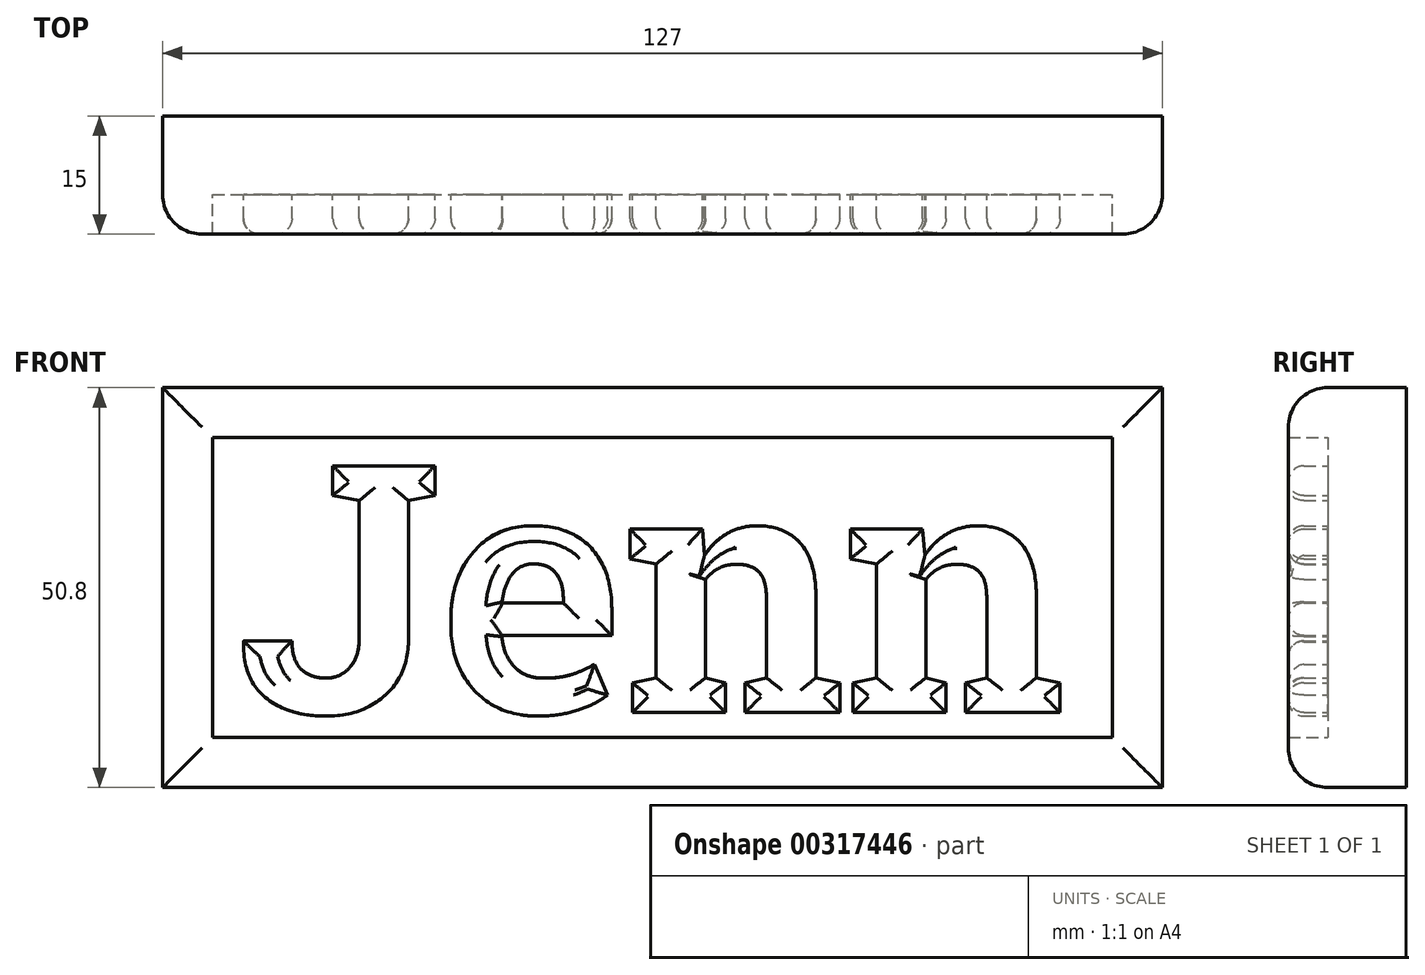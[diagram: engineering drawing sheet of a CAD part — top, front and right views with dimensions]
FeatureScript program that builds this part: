
annotation { "Feature Type Name" : "Feature", "Feature Type Description" : "" }
export const myFeature = defineFeature(function(context is Context, id is Id, definition is map)
    precondition{}
    {
        {
            var Q0;
            Q0=qCreatedBy(makeId("Front.planeOp"),FACE);
            var sketch = newSketch(context, id + "F0", { "sketchPlane" : qUnion([Q0])});
            skText(sketch, "E0", { "text": "Jenn", "fontName": "RobotoSlab-Bold.ttf"});
            const initialGuessF0  = {"E0": [-0.05398, -0.01588, 1, 0, 0.03175]};
            skSetInitialGuess(sketch, initialGuessF0);
            skSolve(sketch);
        }
        {
            var Q0;
            Q0=qCreatedBy(makeId("Front.planeOp"),FACE);
            var sketch = newSketch(context, id + "F1", { "sketchPlane" : qUnion([Q0])});
            skLineSegment(sketch, "E1.bottom", {"start": v(-57.15, 19.05) * mm, "end": v(57.15, 19.05) * mm});
            skLineSegment(sketch, "E1.top", {"start": v(-57.15, -19.05) * mm, "end": v(57.15, -19.05) * mm});
            skLineSegment(sketch, "E1.left", {"start": v(-57.15, 19.05) * mm, "end": v(-57.15, -19.05) * mm});
            skLineSegment(sketch, "E1.right", {"start": v(57.15, 19.05) * mm, "end": v(57.15, -19.05) * mm});
            skLineSegment(sketch, "E2.bottom", {"start": v(-63.5, 25.4) * mm, "end": v(63.5, 25.4) * mm});
            skLineSegment(sketch, "E2.top", {"start": v(-63.5, -25.4) * mm, "end": v(63.5, -25.4) * mm});
            skLineSegment(sketch, "E2.left", {"start": v(-63.5, 25.4) * mm, "end": v(-63.5, -25.4) * mm});
            skLineSegment(sketch, "E2.right", {"start": v(63.5, 25.4) * mm, "end": v(63.5, -25.4) * mm});
            skSolve(sketch);
        }
        {
            var Q0;
            Q0=makeQuery(id+"F1.imprint","IMPRINT",FACE,{"disambiguationData":[TD([[makeQuery(id+"F1.imprint","IMPRINT",EDGE,{"derivedFrom":sQuery(id+"F1.wireOp",EDGE,"E1.bottom")}),-1.0]])]});
            var Q1;
            Q1=makeQuery(id+"F1.imprint","IMPRINT",FACE,{"disambiguationData":[TD([[makeQuery(id+"F1.imprint","IMPRINT",EDGE,{"derivedFrom":sQuery(id+"F1.wireOp",EDGE,"E1.bottom")}),1.0]])]});
            extrude(context, id + "F2", {"entities" : qUnion([Q0, Q1]), "oppositeDirection" : true, "depth" : 10 * mm});
        }
        {
            var Q0;
            Q0=qSketchRegion(id+"F1",true);
            extrude(context, id + "F3", {"entities" : qUnion([Q0]), "operationType" : NewBodyOperationType.ADD, "depth" : 5 * mm});
        }
        {
            var Q0;
            Q0=qSketchRegion(id+"F0",true);
            extrude(context, id + "F4", {"entities" : qUnion([Q0]), "operationType" : NewBodyOperationType.ADD, "depth" : 5 * mm});
        }
        {
            var Q0;
            Q0=makeQuery(id+"F3.opExtrude","CAP_EDGE",EDGE,{"disambiguationData":[OSD([sQuery(id+"F1.wireOp",EDGE,"E2.right")])],"isStart":false});
            var Q1;
            Q1=makeQuery(id+"F3.opExtrude","CAP_EDGE",EDGE,{"disambiguationData":[OSD([sQuery(id+"F1.wireOp",EDGE,"E2.left")])],"isStart":false});
            var Q2;
            Q2=makeQuery(id+"F3.opExtrude","CAP_EDGE",EDGE,{"disambiguationData":[OSD([sQuery(id+"F1.wireOp",EDGE,"E2.bottom")])],"isStart":false});
            var Q3;
            Q3=makeQuery(id+"F3.opExtrude","CAP_EDGE",EDGE,{"disambiguationData":[OSD([sQuery(id+"F1.wireOp",EDGE,"E2.top")])],"isStart":false});
            fillet(context, id + "F5", {"entities" : qUnion([Q0, Q1, Q2, Q3]), "radius" : 5 * mm, "tangentPropagation" : true, "allowEdgeOverflow" : false});
        }
        {
            var Q0;
            Q0=makeQuery(id+"F4.opExtrude","CAP_FACE",FACE,{"disambiguationData":[OSD([sQuery(id+"F0.wireOp",EDGE,"E0.sketch_text.stroke-0"),sQuery(id+"F0.wireOp",EDGE,"E0.sketch_text.stroke-1"),sQuery(id+"F0.wireOp",EDGE,"E0.sketch_text.stroke-2"),sQuery(id+"F0.wireOp",EDGE,"E0.sketch_text.stroke-3"),sQuery(id+"F0.wireOp",EDGE,"E0.sketch_text.stroke-4"),sQuery(id+"F0.wireOp",EDGE,"E0.sketch_text.stroke-5"),sQuery(id+"F0.wireOp",EDGE,"E0.sketch_text.stroke-6"),sQuery(id+"F0.wireOp",EDGE,"E0.sketch_text.stroke-7"),sQuery(id+"F0.wireOp",EDGE,"E0.sketch_text.stroke-8"),sQuery(id+"F0.wireOp",EDGE,"E0.sketch_text.stroke-9"),sQuery(id+"F0.wireOp",EDGE,"E0.sketch_text.stroke-10"),sQuery(id+"F0.wireOp",EDGE,"E0.sketch_text.stroke-11"),sQuery(id+"F0.wireOp",EDGE,"E0.sketch_text.stroke-12"),sQuery(id+"F0.wireOp",EDGE,"E0.sketch_text.stroke-13"),sQuery(id+"F0.wireOp",EDGE,"E0.sketch_text.stroke-14"),sQuery(id+"F0.wireOp",EDGE,"E0.sketch_text.stroke-15"),sQuery(id+"F0.wireOp",EDGE,"E0.sketch_text.stroke-16"),sQuery(id+"F0.wireOp",EDGE,"E0.sketch_text.stroke-17")])],"isStart":false});
            var Q1;
            Q1=makeQuery(id+"F4.opExtrude","CAP_FACE",FACE,{"disambiguationData":[OSD([sQuery(id+"F0.wireOp",EDGE,"E0.sketch_text.stroke-18"),sQuery(id+"F0.wireOp",EDGE,"E0.sketch_text.stroke-19"),sQuery(id+"F0.wireOp",EDGE,"E0.sketch_text.stroke-20"),sQuery(id+"F0.wireOp",EDGE,"E0.sketch_text.stroke-21"),sQuery(id+"F0.wireOp",EDGE,"E0.sketch_text.stroke-22"),sQuery(id+"F0.wireOp",EDGE,"E0.sketch_text.stroke-23"),sQuery(id+"F0.wireOp",EDGE,"E0.sketch_text.stroke-24"),sQuery(id+"F0.wireOp",EDGE,"E0.sketch_text.stroke-25"),sQuery(id+"F0.wireOp",EDGE,"E0.sketch_text.stroke-26"),sQuery(id+"F0.wireOp",EDGE,"E0.sketch_text.stroke-27"),sQuery(id+"F0.wireOp",EDGE,"E0.sketch_text.stroke-28"),sQuery(id+"F0.wireOp",EDGE,"E0.sketch_text.stroke-29"),sQuery(id+"F0.wireOp",EDGE,"E0.sketch_text.stroke-30"),sQuery(id+"F0.wireOp",EDGE,"E0.sketch_text.stroke-31"),sQuery(id+"F0.wireOp",EDGE,"E0.sketch_text.stroke-32"),sQuery(id+"F0.wireOp",EDGE,"E0.sketch_text.stroke-33"),sQuery(id+"F0.wireOp",EDGE,"E0.sketch_text.stroke-34"),sQuery(id+"F0.wireOp",EDGE,"E0.sketch_text.stroke-35"),sQuery(id+"F0.wireOp",EDGE,"E0.sketch_text.stroke-36"),sQuery(id+"F0.wireOp",EDGE,"E0.sketch_text.stroke-37"),sQuery(id+"F0.wireOp",EDGE,"E0.sketch_text.stroke-38"),sQuery(id+"F0.wireOp",EDGE,"E0.sketch_text.stroke-39"),sQuery(id+"F0.wireOp",EDGE,"E0.sketch_text.stroke-40"),sQuery(id+"F0.wireOp",EDGE,"E0.sketch_text.stroke-41")])],"isStart":false});
            var Q2;
            Q2=makeQuery(id+"F4.opExtrude","CAP_FACE",FACE,{"disambiguationData":[OSD([sQuery(id+"F0.wireOp",EDGE,"E0.sketch_text.stroke-42"),sQuery(id+"F0.wireOp",EDGE,"E0.sketch_text.stroke-43"),sQuery(id+"F0.wireOp",EDGE,"E0.sketch_text.stroke-44"),sQuery(id+"F0.wireOp",EDGE,"E0.sketch_text.stroke-45"),sQuery(id+"F0.wireOp",EDGE,"E0.sketch_text.stroke-46"),sQuery(id+"F0.wireOp",EDGE,"E0.sketch_text.stroke-47"),sQuery(id+"F0.wireOp",EDGE,"E0.sketch_text.stroke-48"),sQuery(id+"F0.wireOp",EDGE,"E0.sketch_text.stroke-49"),sQuery(id+"F0.wireOp",EDGE,"E0.sketch_text.stroke-50"),sQuery(id+"F0.wireOp",EDGE,"E0.sketch_text.stroke-51"),sQuery(id+"F0.wireOp",EDGE,"E0.sketch_text.stroke-52"),sQuery(id+"F0.wireOp",EDGE,"E0.sketch_text.stroke-53"),sQuery(id+"F0.wireOp",EDGE,"E0.sketch_text.stroke-54"),sQuery(id+"F0.wireOp",EDGE,"E0.sketch_text.stroke-55"),sQuery(id+"F0.wireOp",EDGE,"E0.sketch_text.stroke-56"),sQuery(id+"F0.wireOp",EDGE,"E0.sketch_text.stroke-57"),sQuery(id+"F0.wireOp",EDGE,"E0.sketch_text.stroke-58"),sQuery(id+"F0.wireOp",EDGE,"E0.sketch_text.stroke-59"),sQuery(id+"F0.wireOp",EDGE,"E0.sketch_text.stroke-60"),sQuery(id+"F0.wireOp",EDGE,"E0.sketch_text.stroke-61"),sQuery(id+"F0.wireOp",EDGE,"E0.sketch_text.stroke-62"),sQuery(id+"F0.wireOp",EDGE,"E0.sketch_text.stroke-63"),sQuery(id+"F0.wireOp",EDGE,"E0.sketch_text.stroke-64"),sQuery(id+"F0.wireOp",EDGE,"E0.sketch_text.stroke-65"),sQuery(id+"F0.wireOp",EDGE,"E0.sketch_text.stroke-66"),sQuery(id+"F0.wireOp",EDGE,"E0.sketch_text.stroke-67")])],"isStart":false});
            var Q3;
            Q3=makeQuery(id+"F4.opExtrude","CAP_FACE",FACE,{"disambiguationData":[OSD([sQuery(id+"F0.wireOp",EDGE,"E0.sketch_text.stroke-68"),sQuery(id+"F0.wireOp",EDGE,"E0.sketch_text.stroke-69"),sQuery(id+"F0.wireOp",EDGE,"E0.sketch_text.stroke-70"),sQuery(id+"F0.wireOp",EDGE,"E0.sketch_text.stroke-71"),sQuery(id+"F0.wireOp",EDGE,"E0.sketch_text.stroke-72"),sQuery(id+"F0.wireOp",EDGE,"E0.sketch_text.stroke-73"),sQuery(id+"F0.wireOp",EDGE,"E0.sketch_text.stroke-74"),sQuery(id+"F0.wireOp",EDGE,"E0.sketch_text.stroke-75"),sQuery(id+"F0.wireOp",EDGE,"E0.sketch_text.stroke-76"),sQuery(id+"F0.wireOp",EDGE,"E0.sketch_text.stroke-77"),sQuery(id+"F0.wireOp",EDGE,"E0.sketch_text.stroke-78"),sQuery(id+"F0.wireOp",EDGE,"E0.sketch_text.stroke-79"),sQuery(id+"F0.wireOp",EDGE,"E0.sketch_text.stroke-80"),sQuery(id+"F0.wireOp",EDGE,"E0.sketch_text.stroke-81"),sQuery(id+"F0.wireOp",EDGE,"E0.sketch_text.stroke-82"),sQuery(id+"F0.wireOp",EDGE,"E0.sketch_text.stroke-83"),sQuery(id+"F0.wireOp",EDGE,"E0.sketch_text.stroke-84"),sQuery(id+"F0.wireOp",EDGE,"E0.sketch_text.stroke-85"),sQuery(id+"F0.wireOp",EDGE,"E0.sketch_text.stroke-86"),sQuery(id+"F0.wireOp",EDGE,"E0.sketch_text.stroke-87"),sQuery(id+"F0.wireOp",EDGE,"E0.sketch_text.stroke-88"),sQuery(id+"F0.wireOp",EDGE,"E0.sketch_text.stroke-89"),sQuery(id+"F0.wireOp",EDGE,"E0.sketch_text.stroke-90"),sQuery(id+"F0.wireOp",EDGE,"E0.sketch_text.stroke-91"),sQuery(id+"F0.wireOp",EDGE,"E0.sketch_text.stroke-92"),sQuery(id+"F0.wireOp",EDGE,"E0.sketch_text.stroke-93")])],"isStart":false});
            fillet(context, id + "F6", {"entities" : qUnion([Q0, Q1, Q2, Q3]), "radius" : 2 * mm, "tangentPropagation" : true, "allowEdgeOverflow" : false});
        }
    });
